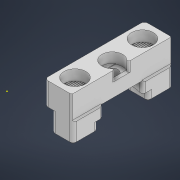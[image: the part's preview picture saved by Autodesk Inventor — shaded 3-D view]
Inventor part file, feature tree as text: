
AUTODESK INVENTOR PART (.ipt)
format: ipt  version: 2022.1 (Build 261234000, 234)  size: 654,848 bytes
history: native  units: mm
features: sketch x14, projected_geometry x12, extrude x11, move_body x9, direct_edit x8, fillet x8, chamfer x5, hole x2, delete_face x2
ambient origin geometry x8: Origin, YZ Plane, XZ Plane, XY Plane, X Axis, Y Axis, Z Axis, Center Point
bodies: Volumenkörper1 (feature_tree)
feature tree (71):
  extrude  "Extrusion1"  Depth=10.0mm
  hole  "Bohrung1"  [1 undecoded]
  hole  "Bohrung2"  [1 undecoded]
  sketch  "Skizze5"  dims[d6=3.12mm d7=6.0mm d8=5.8mm d9=3.2mm d10=90.0deg d11=8.8mm d12=0.0mm d13=11.46mm]
  extrude  "Extrusion2"  Depth=1.0mm
  direct_edit  "Direktbearbeitung1"
  direct_edit  "Direktbearbeitung2"
  fillet  "Rundung2"  Radius=6.0mm
  fillet  "Rundung3"  Radius=1.0mm
  extrude  "Extrusion3"  TaperAngle=0.0deg  [1 undecoded]
  fillet  "Rundung4"  Radius=4.0mm
  chamfer  "Fase1"  Distance=7.0mm
  direct_edit  "Direktbearbeitung3"
  fillet  "Rundung5"  Radius=5.2mm
  extrude  "Extrusion4"  Depth=1.0mm
  extrude  "Extrusion5"  Depth=2.0mm TaperAngle=45.0deg
  chamfer  "Fase2"  Distance=2.0mm
  direct_edit  "Direktbearbeitung4"
  direct_edit  "Direktbearbeitung5"
  direct_edit  "Direktbearbeitung6"
  direct_edit  "Direktbearbeitung7"
  extrude  "Extrusion6"  Depth=1.0mm
  fillet  "Rundung6"  Radius=3.05mm
  chamfer  "Fase3"  Distance=6.1mm
  chamfer  "Fase4"  Distance=2.0mm
  extrude  "Extrusion7"  Depth=1.0mm
  delete_face  "Fläche löschen1"
  extrude  "Extrusion8"  Depth=1.0mm
  fillet  "Rundung7"  Radius=0.1mm
  extrude  "Extrusion9"  Depth=2.0mm
  extrude  "Extrusion10"  Depth=1.0mm
  delete_face  "Fläche löschen2"
  chamfer  "Fase5"  Distance=1.0mm
  fillet  "Rundung8"  Radius=0.1mm
  extrude  "Extrusion11"  TaperAngle=0.0deg  [1 undecoded]
  fillet  "Rundung9"  Radius=0.1mm
  direct_edit  "Direktbearbeitung8"
  sketch  "Skizze1"  dims[d0=10.0mm d1=45.0mm]
  sketch  "Skizze2"  dims[d2=6.8mm d3=0.0mm d4=7.0mm]
  sketch  "Skizze3"  dims[d5=0.0mm]
  sketch  "Skizze6"  dims[d14=22.92mm]
  sketch  "Skizze7"  dims[d15=6.1mm d16=6.0mm d17=5.8mm d18=3.2mm d19=90.0deg d20=3.6mm d21=0.0mm d26=12.0mm d27=6.0mm d28=1.0mm d29=0.0mm]
  projected_geometry  "Projizierte Kontur3"
  projected_geometry  "Projizierte Kontur4"
  sketch  "Skizze8"  dims[d30=0.0mm d31=0.0mm d32=-4.0mm d33=0.0mm d34=0.0mm d35=-4.0mm]
  projected_geometry  "Projizierte Kontur5"
  projected_geometry  "Projizierte Kontur6"
  projected_geometry  "Projizierte Kontur7"
  sketch  "Skizze9"  dims[d36=0.0mm d37=0.0mm d38=-2.0mm d39=4.0mm]
  projected_geometry  "Projizierte Kontur8"
  sketch  "Skizze10"  dims[d40=0.8mm]
  sketch  "Skizze11"  dims[d41=6.0mm]
  sketch  "Skizze12"  dims[d42=7.0mm]
  projected_geometry  "Projizierte Kontur9"
  sketch  "Skizze13"  dims[d43=6.0mm]
  projected_geometry  "Projizierte Kontur10"
  projected_geometry  "Projizierte Kontur11"
  sketch  "Skizze14"  dims[d44=7.0mm]
  projected_geometry  "Projizierte Kontur12"
  sketch  "Skizze15"  dims[d45=7.0mm d46=7.0mm d47=5.2mm d48=0.0mm d49=1.0mm d50=0.6mm d51=2.0mm d52=45.0deg d53=0.0mm d54=0.0mm d55=2.0mm d56=1.0mm d57=3.05mm d58=6.1mm d59=2.0mm d60=0.1mm d61=1.0mm d62=0.1mm d63=2.0mm d64=0.1mm d65=1.0mm d66=0.1mm d67=0.0mm d68=0.1mm d69=0.21mm d70=0.0mm d71=0.2mm d72=0.0mm d73=0.2mm d74=2.0mm d75=45.0deg d76=0.0mm d77=0.0mm d78=-0.2mm d79=-1.0mm d80=0.0mm d81=0.0mm d82=0.0mm d83=2.0mm d84=0.0mm d85=0.0mm d86=-2.0mm d87=0.0mm d88=0.0mm d89=0.0mm d90=1.0mm d91=0.2mm d92=2.0mm d93=45.0deg d94=0.2mm d95=2.0mm d96=45.0deg d97=0.05mm d98=10.0mm d99=0.0mm d100=0.4mm d101=0.0mm d102=0.4mm d103=0.41mm d104=0.05mm d105=0.41mm d106=0.05mm d107=0.41mm d108=0.05mm d109=0.41mm d110=0.05mm d111=0.41mm d112=0.05mm d113=0.41mm d114=0.05mm d115=0.41mm d116=0.05mm d117=0.41mm d118=0.05mm d119=0.41mm d120=0.05mm d121=0.41mm d122=0.05mm d123=0.41mm d124=0.05mm d125=0.41mm d126=0.05mm d127=0.41mm d128=0.05mm d129=0.41mm d130=0.2mm d131=0.0mm d132=0.0mm d133=0.0mm d134=0.4mm d135=2.0mm d136=45.0deg d137=0.8mm d138=0.0mm d139=0.0mm d140=1.0mm d141=0.0mm d142=0.0mm d143=-0.4mm]
  projected_geometry  "Projizierte Kontur13"
  projected_geometry  "Projizierte Kontur14"
  move_body  "Verschieben1"
  move_body  "Verschieben2"
  move_body  "Verschieben3"
  move_body  "Verschieben4"
  move_body  "Verschieben5"
  move_body  "Verschieben6"
  move_body  "Verschieben7"
  move_body  "Verschieben8"
  move_body  "Verschieben9"
note: 4 required parameter values undecoded (feature->parameter linkage not recoverable at this tier; creation-order binding heuristic only, values carry confidence <= 0.55)
